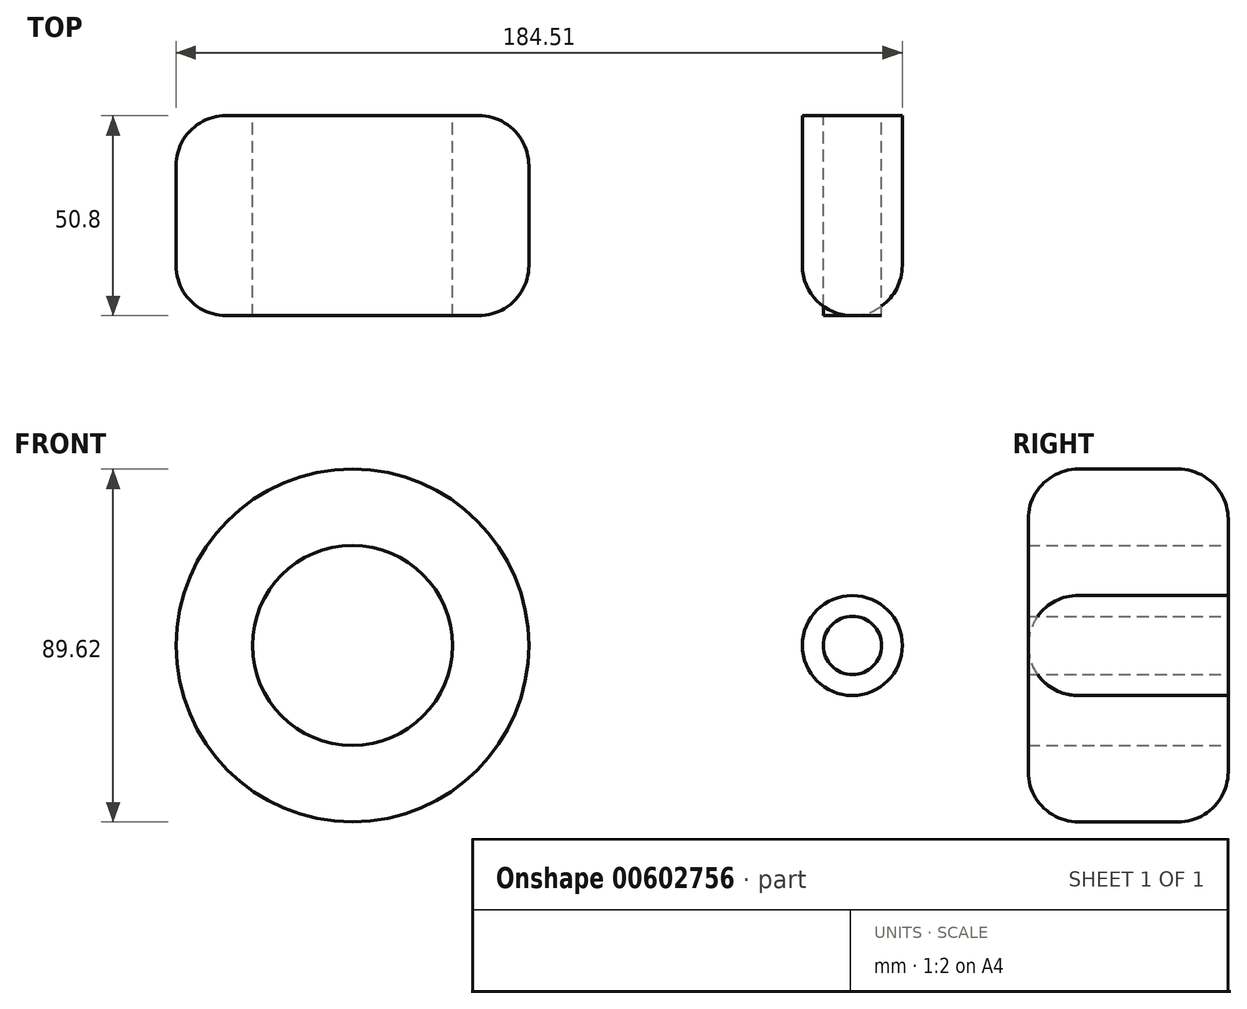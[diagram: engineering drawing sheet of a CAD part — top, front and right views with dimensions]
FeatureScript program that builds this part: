
annotation { "Feature Type Name" : "Feature", "Feature Type Description" : "" }
export const myFeature = defineFeature(function(context is Context, id is Id, definition is map)
    precondition{}
    {
        {
            var Q0;
            Q0=qCreatedBy(makeId("Front.planeOp"),FACE);
            var sketch = newSketch(context, id + "F0", { "sketchPlane" : qUnion([Q0])});
            skCircle(sketch, "E0", {"center": v(0, 0) * mm, "radius": 25.4 * mm});
            skCircle(sketch, "E1", {"center": v(127, 0) * mm, "radius": 12.7 * mm});
            skLineSegment(sketch, "E2", {"start": v(0, 0) * mm, "end": v(127, 0) * mm, "construction": true});
            skLineSegment(sketch, "E3", {"start": v(24.86, 5.2) * mm, "end": v(115.41, 5.2) * mm});
            skSolve(sketch);
        }
        {
            var Q0;
            Q0=makeQuery(id+"F0.imprint","IMPRINT",FACE,{"disambiguationData":[TD([[makeQuery(id+"F0.imprint","IMPRINT",EDGE,{"derivedFrom":sQuery(id+"F0.wireOp",EDGE,"E0")}),1.0]])]});
            var sketch = newSketch(context, id + "F1", { "sketchPlane" : qUnion([Q0])});
            skCircle(sketch, "E4", {"center": v(0, 0) * mm, "radius": 44.8 * mm});
            skCircle(sketch, "E5", {"center": v(127.06, 0) * mm, "radius": 7.41 * mm});
            skLineSegment(sketch, "E6", {"start": v(23.23, -9.16) * mm, "end": v(118.2, -9.16) * mm});
            skSolve(sketch);
        }
        {
            var Q0;
            Q0=makeQuery(id+"F0.imprint","IMPRINT",FACE,{"disambiguationData":[TD([[makeQuery(id+"F0.imprint","IMPRINT",EDGE,{"derivedFrom":sQuery(id+"F0.wireOp",EDGE,"E0")}),1.0]])]});
            var Q1;
            Q1 = qSketchRegion(id + "F0", true);
            var Q2;
            Q2 = qSketchRegion(id + "F1", true);
            extrude(context, id + "F2", {"entities" : qUnion([Q0, Q1, Q2]), "depth" : 50.8 * mm, "offsetDistance" : 25.4 * mm});
        }
        {
            var Q0;
            Q0=makeQuery(id+"F2.opExtrude","CAP_EDGE",EDGE,{"disambiguationData":[OSD([sQuery(id+"F1.wireOp",EDGE,"E4")])],"isStart":false});
            var Q1;
            Q1=makeQuery(id+"F2.opExtrude","CAP_EDGE",EDGE,{"disambiguationData":[OSD([sQuery(id+"F1.wireOp",EDGE,"E4")])],"isStart":true});
            fillet(context, id + "F3", {"entities" : qUnion([Q0, Q1]), "radius" : 12.7 * mm, "tangentPropagation" : true, "allowEdgeOverflow" : false});
        }
        {
            var Q0;
            Q0=makeQuery(id+"F2.opExtrude","CAP_EDGE",EDGE,{"disambiguationData":[OSD([sQuery(id+"F0.wireOp",EDGE,"E1")])],"isStart":false});
            fillet(context, id + "F4", {"entities" : qUnion([Q0]), "radius" : 12.7 * mm, "tangentPropagation" : true, "allowEdgeOverflow" : false});
        }
    });
